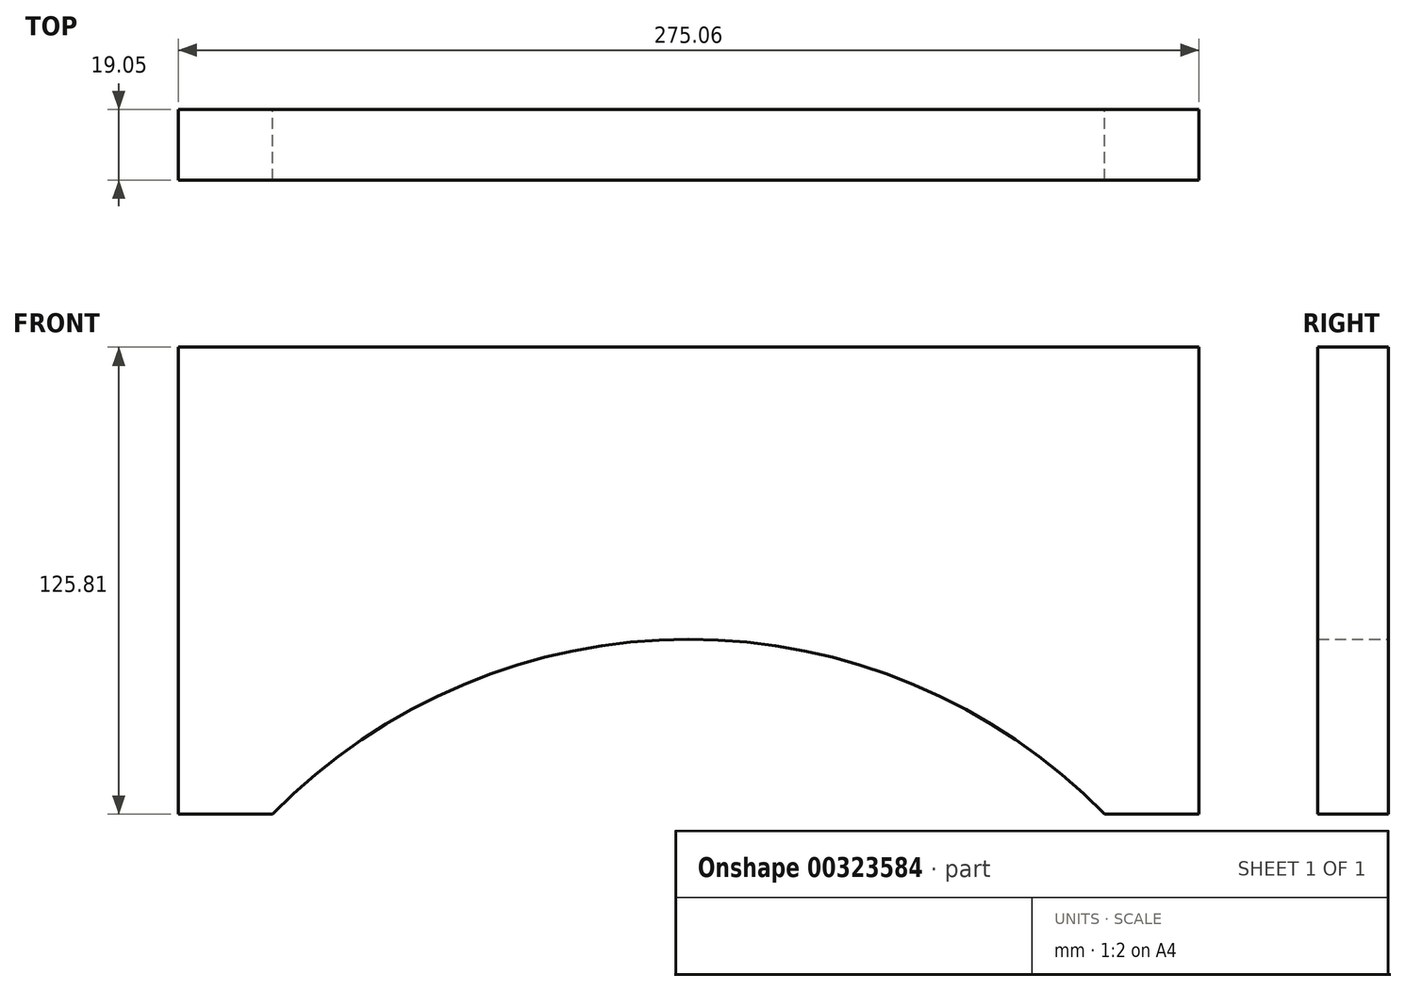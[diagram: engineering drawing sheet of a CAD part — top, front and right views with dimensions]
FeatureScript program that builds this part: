
annotation { "Feature Type Name" : "Feature", "Feature Type Description" : "" }
export const myFeature = defineFeature(function(context is Context, id is Id, definition is map)
    precondition{}
    {
        {
            var Q0;
            Q0=qCreatedBy(makeId("Front.planeOp"),FACE);
            var sketch = newSketch(context, id + "F0", { "sketchPlane" : qUnion([Q0])});
            skLineSegment(sketch, "E0", {"start": v(196.43, 0) * mm, "end": v(-78.63, 0) * mm});
            skLineSegment(sketch, "E1", {"start": v(196.43, 0) * mm, "end": v(196.43, 125.8) * mm});
            skLineSegment(sketch, "E2", {"start": v(0, -72.61) * mm, "end": v(0, 76.65) * mm, "construction": true});
            skLineSegment(sketch, "E3.MirrorCS", {"start": v(69.96, 0) * mm, "end": v(69.96, 21.6) * mm});
            skLineSegment(sketch, "E4", {"start": v(-78.63, 0) * mm, "end": v(-78.63, 125.8) * mm});
            skLineSegment(sketch, "E5", {"start": v(-78.63, 125.8) * mm, "end": v(-53.23, 125.8) * mm});
            skLineSegment(sketch, "E6", {"start": v(171.03, 125.8) * mm, "end": v(196.43, 125.8) * mm});
            skPoint(sketch, "E7.third.point", {"position": v(13.46, -158.17) * mm});
            skPoint(sketch, "E8.first.point", {"position": v(-53.23, 0) * mm});
            skPoint(sketch, "E8.second.point", {"position": v(171.03, 0) * mm});
            skPoint(sketch, "E8.third.point", {"position": v(25.23, -176.3) * mm});
            skLineSegment(sketch, "E9", {"start": v(-53.23, 125.8) * mm, "end": v(171.03, 125.8) * mm});
            skArc(sketch, "E10", {"start": v(171.03, 0) * mm, "mid": v(58.9, 47.1) * mm, "end": v(-53.23, 0) * mm});
            skPoint(sketch, "E10.third.point", {"position": v(9.65, 39.18) * mm});
            skSolve(sketch);
        }
        {
            var Q0;
            Q0 = qSketchRegion(id + "F0", true);
            extrude(context, id + "F1", {"entities" : qUnion([Q0]), "depth" : 19.05 * mm});
        }
        {
            var Q0;
            {var subQ2=sQuery(id+"F0.wireOp",EDGE,"E10");Q0=makeQuery(id+"F0.imprint","IMPRINT",FACE,{"disambiguationData":[TD([[makeQuery(id+"F0.imprint","IMPRINT",EDGE,{"derivedFrom":subQ2}),1.0]])]});}
            extrude(context, id + "F2", {"entities" : qUnion([Q0]), "operationType" : NewBodyOperationType.REMOVE, "depth" : 19.05 * mm});
        }
    });
